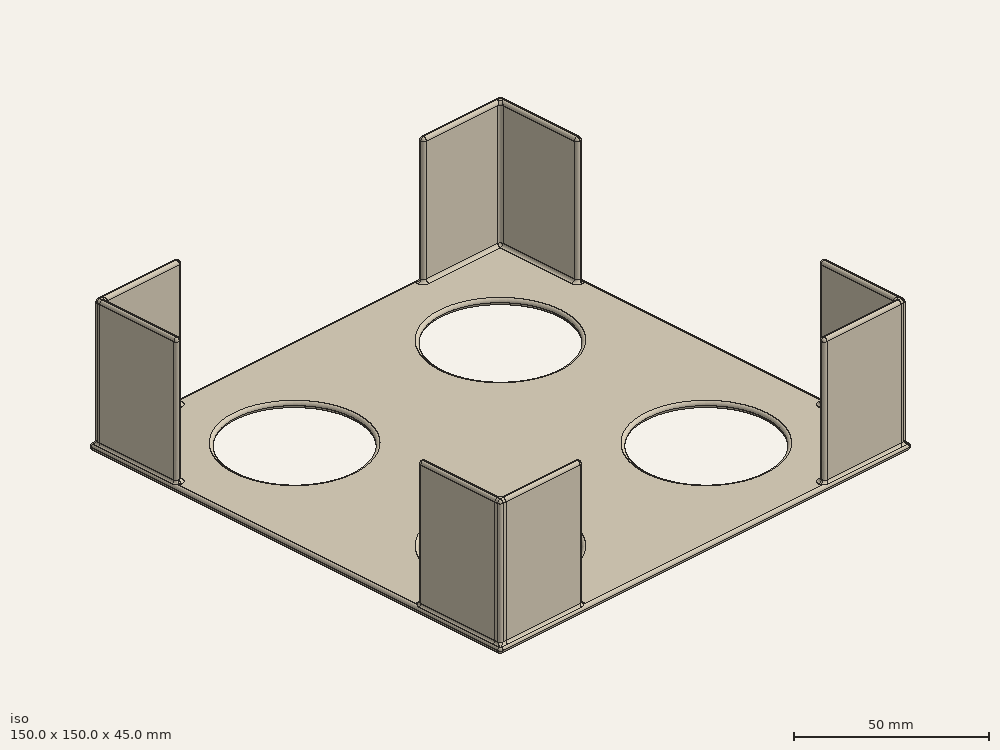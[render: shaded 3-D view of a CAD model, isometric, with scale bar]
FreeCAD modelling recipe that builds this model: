
FCSTD DOCUMENT  (FreeCAD 0.21R33668 +26 (Git))
Label: coffee-organizer
License: Creative Commons Attribution 4.0
LicenseURL: https://creativecommons.org/licenses/by/4.0/
objects: PartDesign::AdditiveBox×9, PartDesign::SubtractiveCylinder×4, PartDesign::Fillet×3, Spreadsheet::Sheet×1, PartDesign::Body×1
note: 33 computed .brp shape members not serialized (recipe doc carries the construction recipe); baked Part::Feature solids carry a one-line shape summary decoded from their .brp

FEATURE [PartDesign::AdditiveBox] Box  label="Base"
  AttacherType = Attacher::AttachEngine3D
  Height = 2.01
  Length = 150
  MapMode = 2
  Support = -> [XY_Plane]
  Width = 150
  expr: Height = Spreadsheet.baseheight
  expr: Length = Spreadsheet.baselength
  expr: Width = Spreadsheet.basewidth
FEATURE [Spreadsheet::Sheet] Spreadsheet
  cells = A1='Base Length; B1(baselength)==150 mm; A2='Base Width; B2(basewidth)==150 mm; A3='Base Height; B3(baseheight)==2.01 mm; A4='Leg Length; B4(leglength)==30 mm; A5='Leg Width; B5(legwidth)==2.01 mm; A6='Leg Height; B6(legheight)==45 mm; A7='Hole Radius; B7(holeradius)==21 mm; A8='Fillet size; B8(filletsize)==1 mm; A9='Right; B9(right)==baselength / 2 - leglength - filletsize; A10='Left; B10(left)==-baselength / 2 + filletsize; A11='Top; B11(top)==basewidth / 2 - legwidth - filletsize; A12='Bottom; B12(bottom)==-basewidth / 2 + filletsize
FEATURE [PartDesign::Fillet] Fillet
  Base = -> Box [Edge1,Edge2,Edge3,Edge4,Edge5,Edge6,Edge7,Edge8,Edge9,Edge10,Edge11,Edge12]
  BaseFeature = -> Box
  Radius = 1
  SupportTransform = false
  UseAllEdges = true
FEATURE [PartDesign::SubtractiveCylinder] Cylinder
  Angle = 360
  AttacherType = Attacher::AttachEngine3D
  AttachmentOffset = pos=(37.5,-37.5,-2.01) rot=(0,0,1;0rad)
  BaseFeature = -> Fillet
  FirstAngle = 0
  Height = 2.01
  MapMode = 5
  Placement = pos=(37.5,37.5,2.01) rot=(1,0,0;3.14159rad)
  Radius = 21
  SecondAngle = 0
  Support = -> [Box]
  expr: .AttachmentOffset.Base.x = Spreadsheet.baselength / 4
  expr: .AttachmentOffset.Base.y = -Spreadsheet.basewidth / 4
  expr: .AttachmentOffset.Base.z = -Height
  expr: Height = Spreadsheet.baseheight
  expr: Radius = Spreadsheet.holeradius
FEATURE [PartDesign::SubtractiveCylinder] Cylinder001
  Angle = 360
  AttacherType = Attacher::AttachEngine3D
  AttachmentOffset = pos=(112.5,37.5,0) rot=(0,0,1;0rad)
  BaseFeature = -> Cylinder
  FirstAngle = 0
  Height = 2.01
  MapMode = 5
  Placement = pos=(112.5,37.5,0) rot=(0,0,1;0rad)
  Radius = 21
  SecondAngle = 0
  Support = -> [XY_Plane]
  expr: .AttachmentOffset.Base.x = Spreadsheet.baselength * 0.75
  expr: .AttachmentOffset.Base.y = Spreadsheet.basewidth / 4
  expr: .AttachmentOffset.Base.z = 0
  expr: Height = Spreadsheet.baseheight
  expr: Radius = Spreadsheet.holeradius
FEATURE [PartDesign::SubtractiveCylinder] Cylinder002
  Angle = 360
  AttacherType = Attacher::AttachEngine3D
  AttachmentOffset = pos=(112.5,112.5,0) rot=(0,0,1;0rad)
  BaseFeature = -> Cylinder001
  FirstAngle = 0
  Height = 2.01
  MapMode = 5
  Placement = pos=(112.5,112.5,0) rot=(0,0,1;0rad)
  Radius = 21
  SecondAngle = 0
  Support = -> [XY_Plane]
  expr: .AttachmentOffset.Base.x = Spreadsheet.baselength * 0.75
  expr: .AttachmentOffset.Base.y = Spreadsheet.baselength * 0.75
  expr: Height = Spreadsheet.baseheight
  expr: Radius = Spreadsheet.holeradius
FEATURE [PartDesign::SubtractiveCylinder] Cylinder003
  Angle = 360
  AttacherType = Attacher::AttachEngine3D
  AttachmentOffset = pos=(37.5,112.5,0) rot=(0,0,1;0rad)
  BaseFeature = -> Cylinder002
  FirstAngle = 0
  Height = 2.01
  MapMode = 5
  Placement = pos=(37.5,112.5,0) rot=(0,0,1;0rad)
  Radius = 21
  SecondAngle = 0
  Support = -> [XY_Plane]
  expr: .AttachmentOffset.Base.x = Spreadsheet.baselength * 0.25
  expr: .AttachmentOffset.Base.y = Spreadsheet.basewidth * 0.75
  expr: Height = Spreadsheet.baseheight
  expr: Radius = Spreadsheet.holeradius
FEATURE [PartDesign::Fillet] Fillet001
  Base = -> Cylinder003 [Edge1,Edge2,Edge3,Edge4,Edge5,Edge6,Edge7,Edge8,Edge9,Edge10,Edge11,Edge12,Edge13,Edge14,Edge15,Edge16,Edge17,Edge18,Edge19,Edge20,Edge21,Edge22,Edge23,Edge24,Edge25,Edge26,Edge27,Edge28,Edge29,Edge30,Edge31,Edge32,Edge33,Edge34,Edge35,Edge36,Edge37,Edge38,Edge39,Edge40,+28 more]
  BaseFeature = -> Cylinder003
  Placement = pos=(37.5,112.5,0) rot=(0,0,1;0rad)
  Radius = 1
  SupportTransform = false
  UseAllEdges = true
FEATURE [PartDesign::AdditiveBox] Box001
  AttacherType = Attacher::AttachEngine3D
  AttachmentOffset = pos=(1,1,0) rot=(0,0,1;0rad)
  BaseFeature = -> Fillet001
  Height = 45
  Length = 30
  MapMode = 2
  Placement = pos=(1,1,0) rot=(0,0,1;0rad)
  Support = -> [XY_Plane]
  Width = 2.01
  expr: Height = Spreadsheet.legheight
  expr: Length = Spreadsheet.leglength
  expr: Width = Spreadsheet.legwidth
FEATURE [PartDesign::AdditiveBox] Box002
  AttacherType = Attacher::AttachEngine3D
  AttachmentOffset = pos=(1,31,0) rot=(0,0,1;4.71239rad)
  BaseFeature = -> Box001
  Height = 45
  Length = 30
  MapMode = 2
  Placement = pos=(1,31,0) rot=(0,0,1;4.71239rad)
  Support = -> [XY_Plane]
  Width = 2.01
  expr: .AttachmentOffset.Base.y = Length + 1 mm
  expr: Height = Spreadsheet.legheight
  expr: Length = Spreadsheet.leglength
  expr: Width = Spreadsheet.legwidth
FEATURE [PartDesign::AdditiveBox] Box003
  AttacherType = Attacher::AttachEngine3D
  AttachmentOffset = pos=(119,1,0) rot=(0,0,1;0rad)
  BaseFeature = -> Box002
  Height = 45
  Length = 30
  MapMode = 5
  Placement = pos=(119,1,0) rot=(0,0,1;0rad)
  Support = -> [XY_Plane]
  Width = 2.01
  expr: .AttachmentOffset.Base.x = Spreadsheet.baselength - Length - 1 mm
  expr: Height = Spreadsheet.legheight
  expr: Length = Spreadsheet.leglength
  expr: Width = Spreadsheet.legwidth
FEATURE [PartDesign::AdditiveBox] Box004
  AttacherType = Attacher::AttachEngine3D
  AttachmentOffset = pos=(149,1,0) rot=(0,0,1;1.5708rad)
  BaseFeature = -> Box003
  Height = 45
  Length = 30
  MapMode = 5
  Placement = pos=(149,1,0) rot=(0,0,1;1.5708rad)
  Support = -> [XY_Plane]
  Width = 2.01
  expr: .AttachmentOffset.Base.x = Spreadsheet.baselength - 1 mm
  expr: Height = Spreadsheet.legheight
  expr: Length = Spreadsheet.leglength
  expr: Width = Spreadsheet.legwidth
FEATURE [PartDesign::AdditiveBox] Box005
  AttacherType = Attacher::AttachEngine3D
  AttachmentOffset = pos=(1,146.99,0) rot=(0,0,1;0rad)
  BaseFeature = -> Box004
  Height = 45
  Length = 30
  MapMode = 5
  Placement = pos=(1,146.99,0) rot=(0,0,1;0rad)
  Support = -> [XY_Plane]
  Width = 2.01
  expr: .AttachmentOffset.Base.y = Spreadsheet.basewidth - Width - 1 mm
  expr: Height = Spreadsheet.legheight
  expr: Length = Spreadsheet.leglength
  expr: Width = Spreadsheet.legwidth
FEATURE [PartDesign::AdditiveBox] Box006
  AttacherType = Attacher::AttachEngine3D
  AttachmentOffset = pos=(1,149,0) rot=(0,0,1;4.71239rad)
  BaseFeature = -> Box005
  Height = 45
  Length = 30
  MapMode = 5
  Placement = pos=(1,149,0) rot=(0,0,1;4.71239rad)
  Support = -> [XY_Plane]
  Width = 2.01
  expr: .AttachmentOffset.Base.y = Spreadsheet.baselength - 1 mm
  expr: Height = Spreadsheet.legheight
  expr: Length = Spreadsheet.leglength
  expr: Width = Spreadsheet.legwidth
FEATURE [PartDesign::AdditiveBox] Box007
  AttacherType = Attacher::AttachEngine3D
  AttachmentOffset = pos=(119,146.99,0) rot=(0,0,1;0rad)
  BaseFeature = -> Box006
  Height = 45
  Length = 30
  MapMode = 5
  Placement = pos=(119,146.99,0) rot=(0,0,1;0rad)
  Support = -> [XY_Plane]
  Width = 2.01
  expr: .AttachmentOffset.Base.x = Spreadsheet.baselength - Length - 1 mm
  expr: .AttachmentOffset.Base.y = Spreadsheet.basewidth - Width - 1 mm
  expr: Height = Spreadsheet.legheight
  expr: Length = Spreadsheet.leglength
  expr: Width = Spreadsheet.legwidth
FEATURE [PartDesign::AdditiveBox] Box008
  AttacherType = Attacher::AttachEngine3D
  AttachmentOffset = pos=(146.99,149,0) rot=(0,0,1;4.71239rad)
  BaseFeature = -> Box007
  Height = 45
  Length = 30
  MapMode = 5
  Placement = pos=(146.99,149,0) rot=(0,0,1;4.71239rad)
  Support = -> [XY_Plane]
  Width = 2.01
  expr: .AttachmentOffset.Base.x = Spreadsheet.baselength - Width - 1 mm
  expr: .AttachmentOffset.Base.y = Spreadsheet.basewidth - 1 mm
  expr: Height = Spreadsheet.legheight
  expr: Length = Spreadsheet.leglength
  expr: Width = Spreadsheet.legwidth
FEATURE [PartDesign::Fillet] Fillet002
  Base = -> Box008 [Edge1,Edge2,Edge3,Edge4,Edge5,Edge6,Edge7,Edge8,Edge9,Edge10,Edge11,Edge12,Edge13,Edge14,Edge15,Edge16,Edge17,Edge18,Edge19,Edge20,Edge21,Edge22,Edge23,Edge24,Edge25,Edge26,Edge27,Edge28,Edge29,Edge30,Edge31,Edge32,Edge33,Edge34,Edge35,Edge36,Edge37,Edge38,Edge39,Edge40,+188 more]
  BaseFeature = -> Box008
  Placement = pos=(146.99,149,0) rot=(0,0,1;4.71239rad)
  Radius = 1
  SupportTransform = false
  UseAllEdges = true
FEATURE [PartDesign::Body] Body
  Group = -> [Box,Fillet,Cylinder,Cylinder001,Cylinder002,Cylinder003,Fillet001,Box001,Box002,Box003,Box004,Box005,Box006,Box007,Box008,Fillet002]
  Origin = -> Origin
  Tip = -> Fillet002
